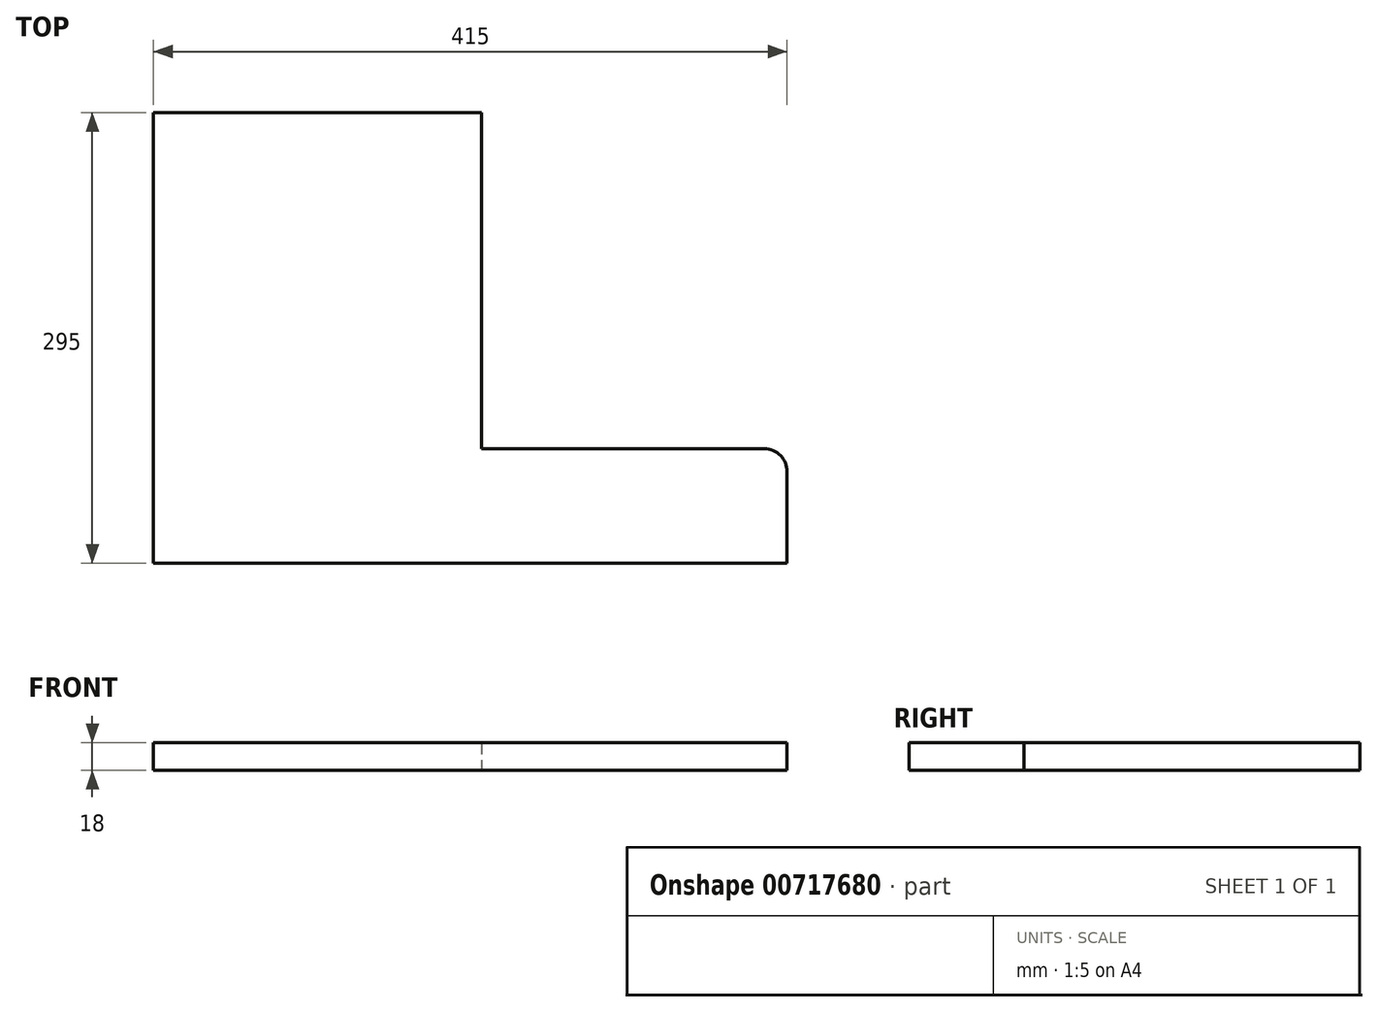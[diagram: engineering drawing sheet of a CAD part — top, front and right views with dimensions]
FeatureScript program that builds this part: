
annotation { "Feature Type Name" : "Feature", "Feature Type Description" : "" }
export const myFeature = defineFeature(function(context is Context, id is Id, definition is map)
    precondition{}
    {
        {
            var Q0;
            Q0=qCreatedBy(makeId("Top.planeOp"),FACE);
            var sketch = newSketch(context, id + "F0", { "sketchPlane" : qUnion([Q0])});
            skLineSegment(sketch, "E0.bottom", {"start": v(0, 0) * mm, "end": v(415, 0) * mm});
            skLineSegment(sketch, "E0.top", {"start": v(0, 295) * mm, "end": v(215, 295) * mm});
            skLineSegment(sketch, "E0.left", {"start": v(0, 0) * mm, "end": v(0, 295) * mm});
            skLineSegment(sketch, "E0.right", {"start": v(415, 0) * mm, "end": v(415, 60) * mm});
            skLineSegment(sketch, "E1.top", {"start": v(400, 75) * mm, "end": v(215, 75) * mm});
            skLineSegment(sketch, "E1.right", {"start": v(215, 295) * mm, "end": v(215, 75) * mm});
            skPoint(sketch, "E2.visualSharp", {"position": v(415, 75) * mm});
            skArc(sketch, "E2.filletArc", {"start": v(415, 60) * mm, "mid": v(410.6, 70.6) * mm, "end": v(400, 75) * mm});
            skSolve(sketch);
        }
        {
            var Q0;
            Q0=makeQuery(id+"F0.imprint","IMPRINT",FACE,{"disambiguationData":[TD([[makeQuery(id+"F0.imprint","IMPRINT",EDGE,{"derivedFrom":sQuery(id+"F0.wireOp",EDGE,"E0.bottom")}),1.0]])]});
            extrude(context, id + "F1", {"entities" : qUnion([Q0]), "depth" : 18 * mm, "offsetDistance" : 25 * mm});
        }
    });
